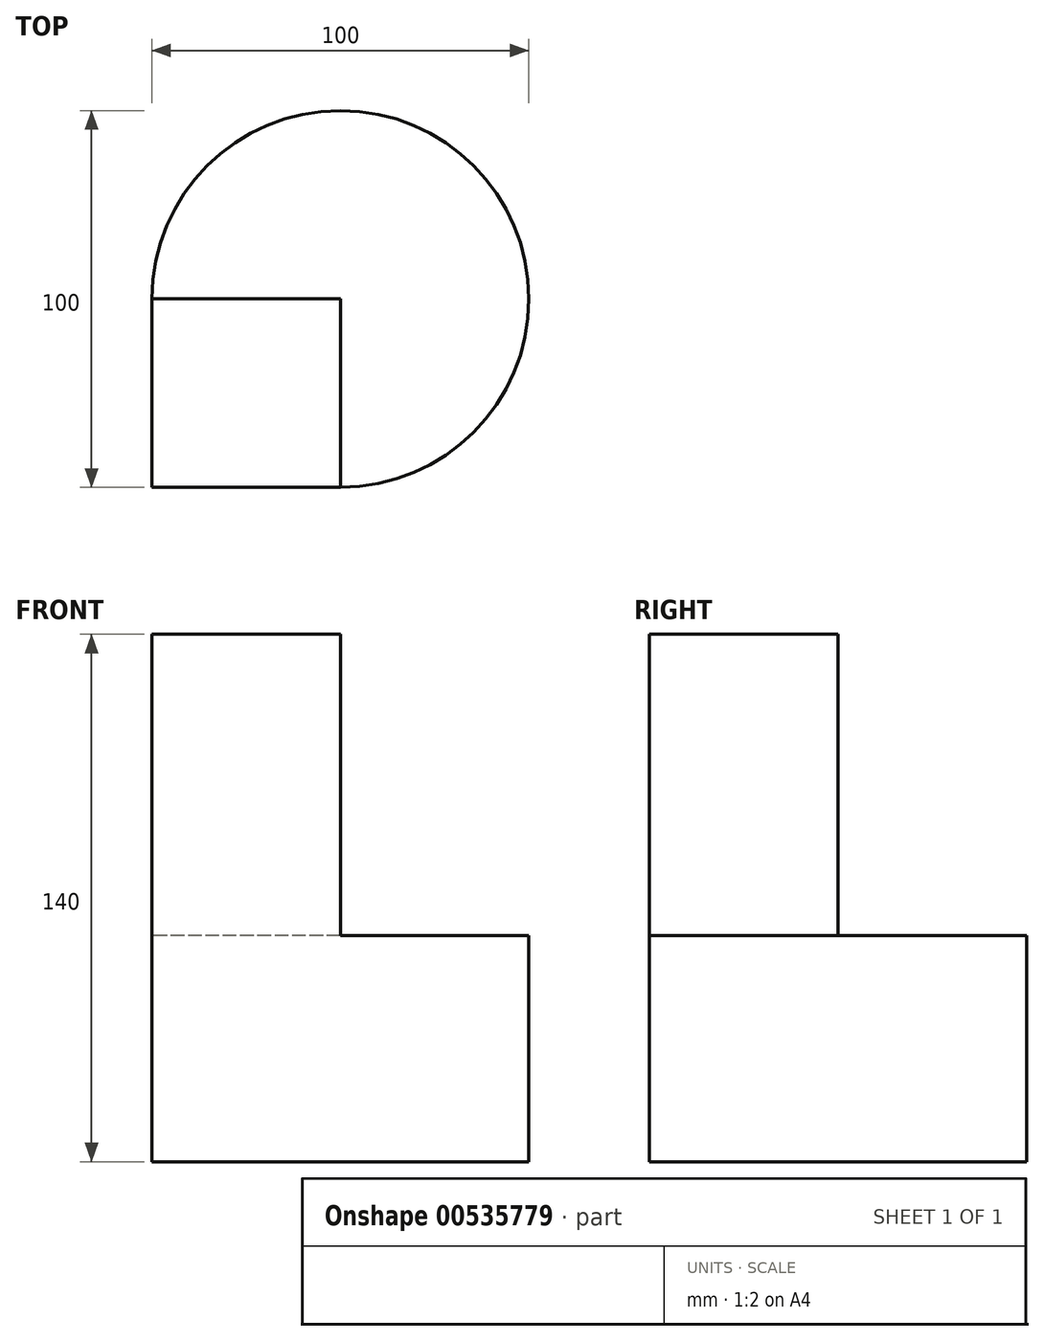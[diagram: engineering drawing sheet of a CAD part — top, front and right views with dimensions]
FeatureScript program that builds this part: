
annotation { "Feature Type Name" : "Feature", "Feature Type Description" : "" }
export const myFeature = defineFeature(function(context is Context, id is Id, definition is map)
    precondition{}
    {
        {
            var Q0;
            Q0=qCreatedBy(makeId("Top.planeOp"),FACE);
            var sketch = newSketch(context, id + "F0", { "sketchPlane" : qUnion([Q0])});
            skCircle(sketch, "E0", {"center": v(0, 0) * mm, "radius": 50 * mm});
            skSolve(sketch);
        }
        {
            var Q0;
            Q0 = qSketchRegion(id + "F0", true);
            extrude(context, id + "F1", {"entities" : qUnion([Q0]), "depth" : 60 * mm, "offsetDistance" : 25 * mm});
        }
        {
            var Q0;
            Q0=makeQuery(id+"F1.opExtrude","CAP_FACE",FACE,{"disambiguationData":[OSD([sQuery(id+"F0.wireOp",EDGE,"E0")])],"isStart":false});
            var sketch = newSketch(context, id + "F2", { "sketchPlane" : qUnion([Q0])});
            skLineSegment(sketch, "E1", {"start": v(0, 0) * mm, "end": v(0, -50) * mm});
            skLineSegment(sketch, "E2", {"start": v(0, 0) * mm, "end": v(-50, 0) * mm});
            skCircle(sketch, "E3", {"center": v(0, 0) * mm, "radius": 50 * mm});
            skSolve(sketch);
        }
        {
            var Q0;
            {var subQ0=sQuery(id+"F2.wireOp",EDGE,"E1");Q0=makeQuery(id+"F2.imprint","IMPRINT",FACE,{"disambiguationData":[TD([[makeQuery(id+"F2.imprint","IMPRINT",EDGE,{"derivedFrom":subQ0}),-1.0]])]});}
            extrude(context, id + "F3", {"entities" : qUnion([Q0]), "operationType" : NewBodyOperationType.REMOVE, "oppositeDirection" : true, "depth" : 80 * mm, "offsetDistance" : 25 * mm});
        }
        {
            var Q0;
            Q0=qCreatedBy(makeId("Top.planeOp"),FACE);
            var sketch = newSketch(context, id + "F4", { "sketchPlane" : qUnion([Q0])});
            skLineSegment(sketch, "E4.bottom", {"start": v(0, 0) * mm, "end": v(-50, 0) * mm});
            skLineSegment(sketch, "E4.top", {"start": v(0, -50) * mm, "end": v(-50, -50) * mm});
            skLineSegment(sketch, "E4.left", {"start": v(0, 0) * mm, "end": v(0, -50) * mm});
            skLineSegment(sketch, "E4.right", {"start": v(-50, 0) * mm, "end": v(-50, -50) * mm});
            skSolve(sketch);
        }
        {
            var Q0;
            Q0 = qSketchRegion(id + "F4", true);
            extrude(context, id + "F5", {"entities" : qUnion([Q0]), "operationType" : NewBodyOperationType.ADD, "depth" : 140 * mm, "offsetDistance" : 25 * mm});
        }
    });
